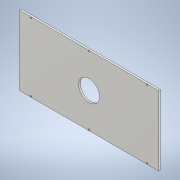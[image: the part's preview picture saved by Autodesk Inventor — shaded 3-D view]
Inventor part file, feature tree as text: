
AUTODESK INVENTOR PART (.ipt)
format: ipt  version: 2021 (Build 250183000, 183)  size: 128,000 bytes
history: native  units: mm
features: extrude x2, sketch x2, other x1, chamfer x1
ambient origin geometry x8: Origin, YZ Plane, XZ Plane, XY Plane, X Axis, Y Axis, Z Axis, Center Point
bodies: Body1 (feature_tree)
feature tree (6):
  other  "Sólido1"
  extrude  "Extrusão1"  Depth=300.0mm
  extrude  "Extrusão2"  Depth=8.0mm TaperAngle=0.0deg
  chamfer  "Chanfro1"  Distance=292.0mm
  sketch  "Esboço1"  dims[d0=600.0mm d1=300.0mm]
  sketch  "Esboço2"  dims[d2=90.0mm d3=8.0mm d4=0.0mm d5=292.0mm d7=4.0mm d8=4.0mm d9=4.0mm d10=4.0mm d11=4.0mm d12=4.0mm d13=10.0mm d14=0.0mm d15=1.0mm d16=2.0mm d17=45.0deg]
